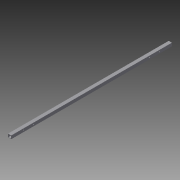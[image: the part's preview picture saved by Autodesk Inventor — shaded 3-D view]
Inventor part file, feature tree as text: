
AUTODESK INVENTOR PART (.ipt)
format: ipt  version: 2016 (Build 200138000, 138)  size: 122,368 bytes
history: native  units: in
note: dims shown in document units (in); Inventor stores cm internally (conversion verified against a paired STEP export)
features: reference x8, sketch x6, hole x4, extrude x1
ambient origin geometry x8: Origin, YZ Plane, XZ Plane, XY Plane, X Axis, Y Axis, Z Axis, Center Point
bodies: Solid1 (feature_tree)
feature tree (19):
  extrude  "Extrusion1"  Depth=1.0in
  hole  "Hole1"  [1 undecoded]
  sketch  "Sketch3"  dims[d5=0.266in d6=0.75in d7=0.375in d8=0.25in d9=0.5635in d10=0.5in d11=0.8108in]
  hole  "Hole2"  [1 undecoded]
  hole  "Hole3"  [1 undecoded]
  hole  "Hole4"  [1 undecoded]
  sketch  "Sketch1"  dims[d0=1.0in d1=1.0in]
  sketch  "Sketch2"  dims[d2=0.12in d3=50.0in d4=0.0in]
  reference  "Reference1"
  reference  "Reference2"
  reference  "Reference3"
  reference  "Reference4"
  sketch  "Sketch5"  dims[d12=0.5in d13=0.75in d14=0.375in d15=0.25in d16=0.5635in d17=0.125in d18=0.8108in d19=4.75in]
  sketch  "Sketch6"  dims[d20=4.5in d21=4.75in]
  sketch  "Sketch7"  dims[d22=4.5in d23=0.2656in d24=0.75in d25=0.375in d26=0.25in d27=0.5635in d28=0.125in d29=0.8108in d31=0.5in d32=0.75in d33=0.375in d34=0.25in d35=0.5635in d36=0.125in d37=0.8108in]
  reference  "Reference5"
  reference  "Reference6"
  reference  "Reference7"
  reference  "Reference8"
note: 4 required parameter values undecoded (feature->parameter linkage not recoverable at this tier; creation-order binding heuristic only, values carry confidence <= 0.55)
